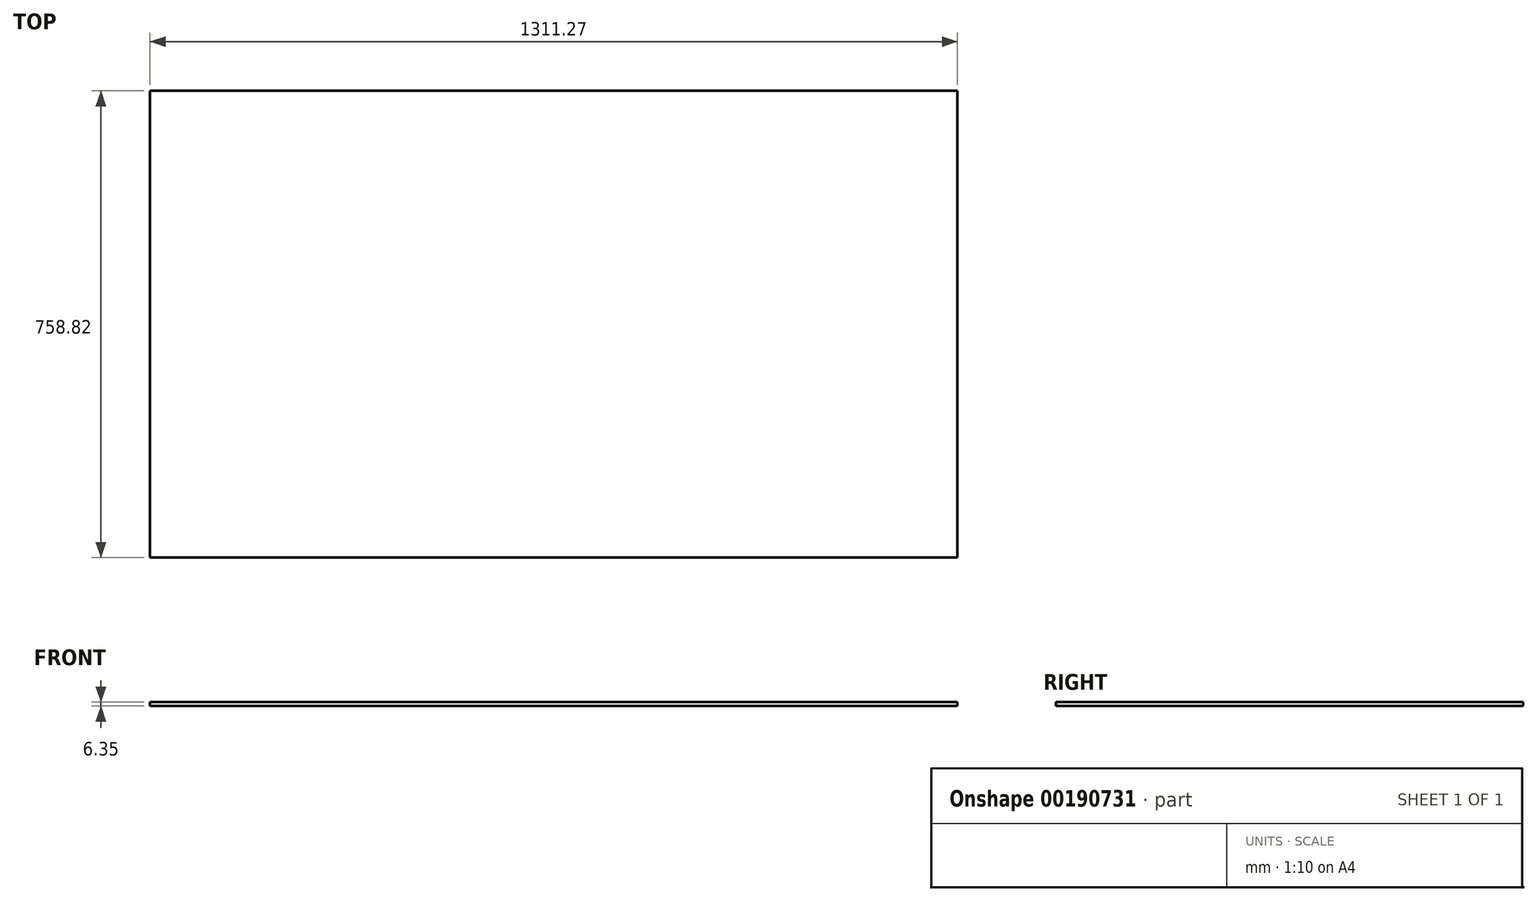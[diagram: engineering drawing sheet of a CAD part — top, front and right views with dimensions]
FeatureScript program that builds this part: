
annotation { "Feature Type Name" : "Feature", "Feature Type Description" : "" }
export const myFeature = defineFeature(function(context is Context, id is Id, definition is map)
    precondition{}
    {
        {
            var Q0;
            Q0=qCreatedBy(makeId("Top.planeOp"),FACE);
            var sketch = newSketch(context, id + "F0", { "sketchPlane" : qUnion([Q0])});
            skLineSegment(sketch, "E0.bottom", {"start": v(0, 0) * mm, "end": v(1311.28, 0) * mm});
            skLineSegment(sketch, "E0.top", {"start": v(0, 758.83) * mm, "end": v(1311.28, 758.83) * mm});
            skLineSegment(sketch, "E0.left", {"start": v(0, 0) * mm, "end": v(0, 758.83) * mm});
            skLineSegment(sketch, "E0.right", {"start": v(1311.28, 0) * mm, "end": v(1311.27, 758.83) * mm});
            skSolve(sketch);
        }
        {
            var Q0;
            Q0 = qSketchRegion(id + "F0", true);
            extrude(context, id + "F1", {"entities" : qUnion([Q0]), "depth" : 6.35 * mm});
        }
    });
